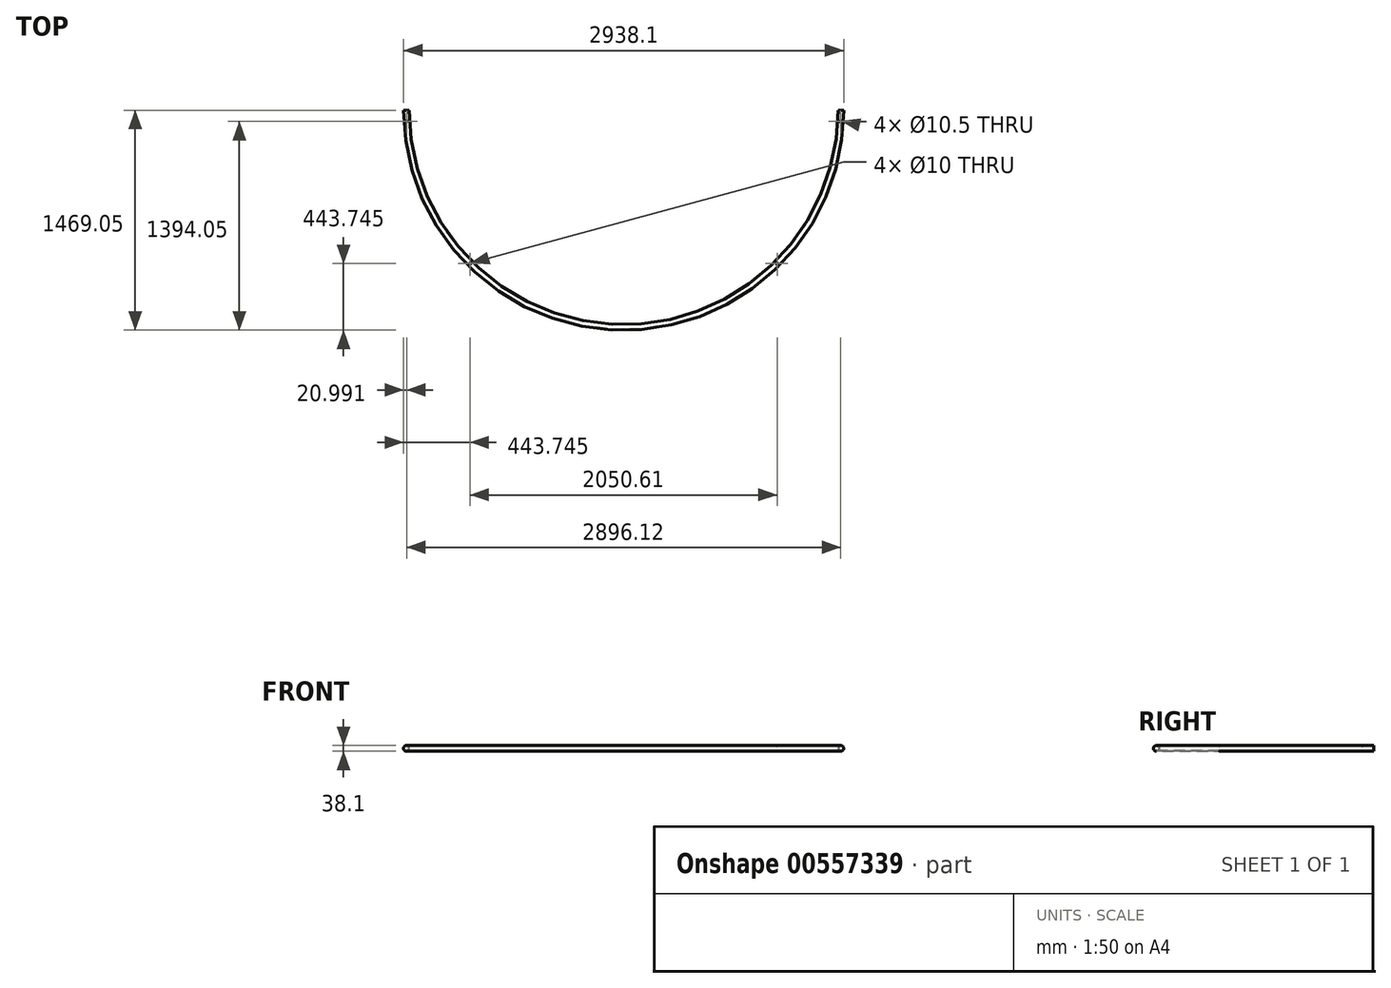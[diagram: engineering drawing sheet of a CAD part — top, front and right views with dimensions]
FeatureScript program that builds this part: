
annotation { "Feature Type Name" : "Feature", "Feature Type Description" : "" }
export const myFeature = defineFeature(function(context is Context, id is Id, definition is map)
    precondition{}
    {
        {
            var Q0;
            Q0=qCreatedBy(makeId("Front.planeOp"),FACE);
            var sketch = newSketch(context, id + "F0", { "sketchPlane" : qUnion([Q0])});
            skCircle(sketch, "E0", {"center": v(-1450, 0) * mm, "radius": 19.05 * mm});
            skCircle(sketch, "E1", {"center": v(-1450, 0) * mm, "radius": 15.85 * mm});
            skLineSegment(sketch, "E2", {"start": v(0, 0) * mm, "end": v(0, 380.17) * mm, "construction": true});
            skSolve(sketch);
        }
        {
            var Q0;
            Q0=qSketchRegion(id+"F0",true);
            var Q1;
            Q1=sQuery(id+"F0.wireOp",EDGE,"E2");
            revolve(context, id + "F1", {"entities" : qUnion([Q0]), "axis" : qUnion([Q1]), "revolveType" : RevolveType.ONE_DIRECTION, "angle" : 180 * degree});
        }
        {
            var Q0;
            Q0=qCreatedBy(makeId("Top.planeOp"),FACE);
            var sketch = newSketch(context, id + "F2", { "sketchPlane" : qUnion([Q0])});
            skArc(sketch, "E3", {"start": v(-1450, 0) * mm, "mid": v(0, -1450) * mm, "end": v(1450, 0) * mm, "construction": true});
            skCircle(sketch, "E4", {"center": v(-1448.06, -75) * mm, "radius": 5.25 * mm});
            skLineSegment(sketch, "E5", {"start": v(0, 0) * mm, "end": v(0, -1450) * mm, "construction": true});
            skCircle(sketch, "E6.MirrorC", {"center": v(1448.06, -75) * mm, "radius": 5.25 * mm});
            skSolve(sketch);
        }
        {
            var Q0;
            Q0=qSketchRegion(id+"F2",true);
            extrude(context, id + "F3", {"entities" : qUnion([Q0]), "operationType" : NewBodyOperationType.REMOVE, "endBound" : BoundingType.THROUGH_ALL, "oppositeDirection" : true, "depth" : 25 * mm, "offsetDistance" : 25 * mm, "hasSecondDirection" : true, "secondDirectionBound" : BoundingType.THROUGH_ALL, "secondDirectionOppositeDirection" : false, "secondDirectionDepth" : 25 * mm});
        }
        {
            var Q0;
            Q0=qCreatedBy(makeId("Top.planeOp"),FACE);
            var sketch = newSketch(context, id + "F4", { "sketchPlane" : qUnion([Q0])});
            skCircle(sketch, "E7", {"center": v(-1025.3, -1025.3) * mm, "radius": 5 * mm});
            skLineSegment(sketch, "E8", {"start": v(-1025.3, -1025.3) * mm, "end": v(0, 0) * mm, "construction": true});
            skCircle(sketch, "E9.MirrorC", {"center": v(1025.3, -1025.3) * mm, "radius": 5 * mm});
            skSolve(sketch);
        }
        {
            var Q0;
            Q0 = qSketchRegion(id + "F4", true);
            extrude(context, id + "F5", {"entities" : qUnion([Q0]), "operationType" : NewBodyOperationType.REMOVE, "endBound" : BoundingType.THROUGH_ALL, "oppositeDirection" : true, "depth" : 25 * mm, "offsetDistance" : 25 * mm, "hasSecondDirection" : true, "secondDirectionBound" : BoundingType.THROUGH_ALL, "secondDirectionOppositeDirection" : false, "secondDirectionDepth" : 25 * mm});
        }
    });
